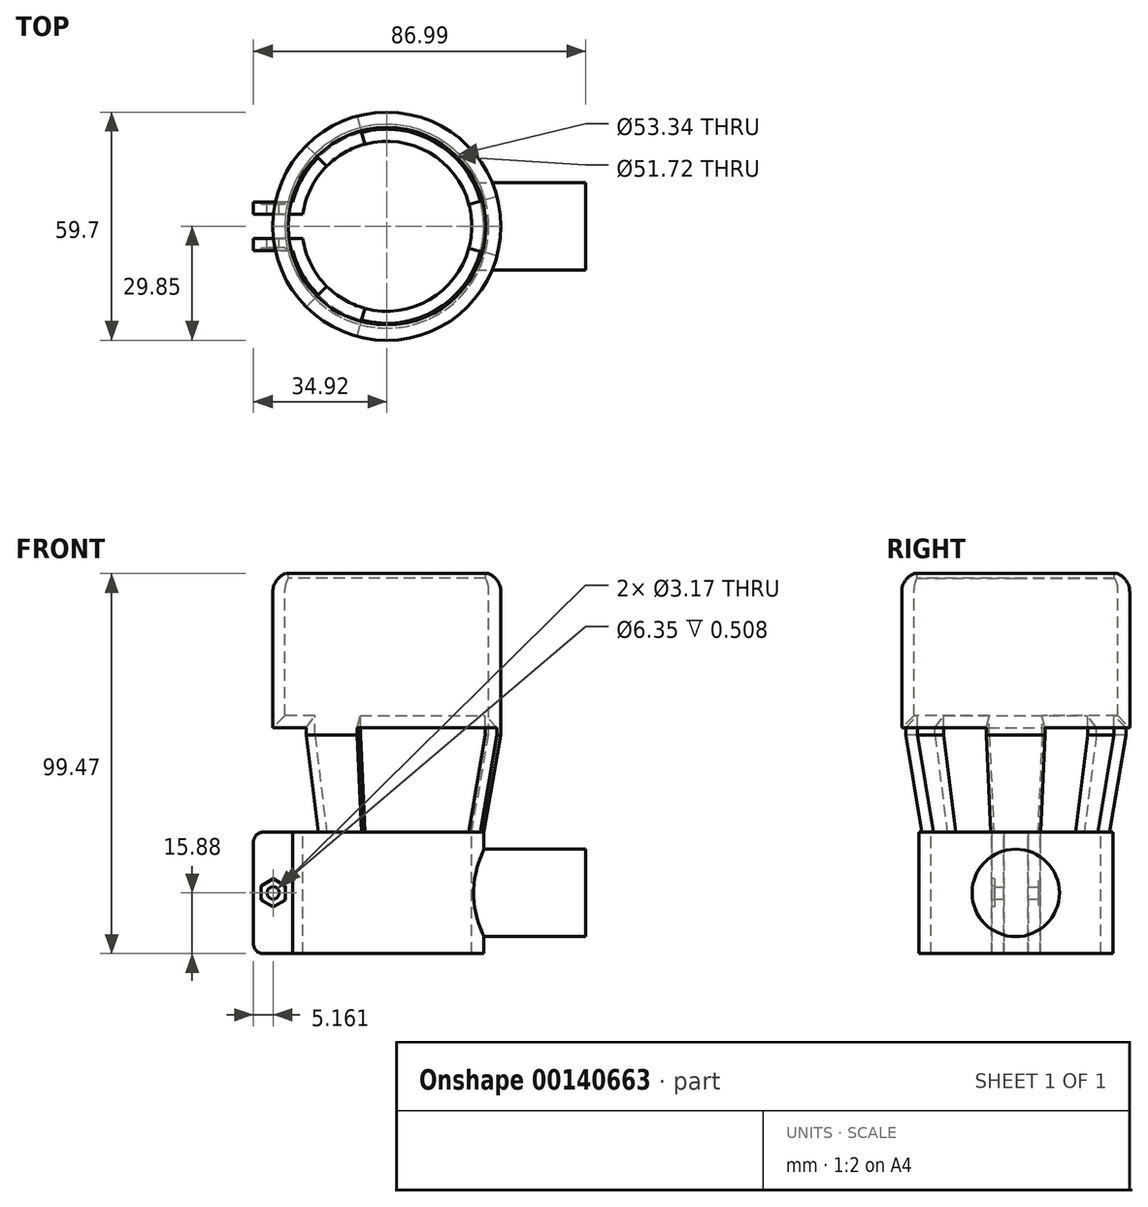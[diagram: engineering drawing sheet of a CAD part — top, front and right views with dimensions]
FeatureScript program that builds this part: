
annotation { "Feature Type Name" : "Feature", "Feature Type Description" : "" }
export const myFeature = defineFeature(function(context is Context, id is Id, definition is map)
    precondition{}
    {
        {
            var Q0;
            Q0=qCreatedBy(makeId("Front.planeOp"),FACE);
            var sketch = newSketch(context, id + "F0", { "sketchPlane" : qUnion([Q0])});
            skLineSegment(sketch, "E0.bottom", {"start": v(22.23, -15.87) * mm, "end": v(-22.23, -15.88) * mm});
            skLineSegment(sketch, "E0.top", {"start": v(22.22, 15.88) * mm, "end": v(-22.23, 15.87) * mm});
            skLineSegment(sketch, "E0.left", {"start": v(22.23, -15.87) * mm, "end": v(22.22, 15.88) * mm});
            skLineSegment(sketch, "E0.right", {"start": v(-22.23, -15.88) * mm, "end": v(-22.23, 15.88) * mm});
            skPoint(sketch, "E0.middle", {"position": v(0, 0) * mm});
            skLineSegment(sketch, "E1.top", {"start": v(26.67, 79.38) * mm, "end": v(-26.67, 79.38) * mm});
            skLineSegment(sketch, "E1.left", {"start": v(26.67, 41.28) * mm, "end": v(26.67, 79.38) * mm});
            skLineSegment(sketch, "E1.right", {"start": v(-26.67, 41.28) * mm, "end": v(-26.67, 79.38) * mm});
            skPoint(sketch, "E1.middle", {"position": v(0, 60.33) * mm});
            skPoint(sketch, "E2.middle", {"position": v(0, 38.1) * mm});
            skLineSegment(sketch, "E3", {"start": v(26.67, 79.38) * mm, "end": v(29.85, 79.38) * mm});
            skLineSegment(sketch, "E4", {"start": v(29.85, 79.38) * mm, "end": v(29.85, 41.28) * mm});
            skLineSegment(sketch, "E5", {"start": v(29.85, 41.27) * mm, "end": v(26.67, 41.27) * mm});
            skLineSegment(sketch, "E6", {"start": v(22.22, 15.88) * mm, "end": v(25.4, 15.88) * mm});
            skLineSegment(sketch, "E7", {"start": v(25.4, 15.88) * mm, "end": v(25.4, -15.87) * mm});
            skLineSegment(sketch, "E8", {"start": v(25.4, -15.87) * mm, "end": v(22.23, -15.87) * mm});
            skLineSegment(sketch, "E9", {"start": v(0, 79.38) * mm, "end": v(0, -15.88) * mm, "construction": true});
            skLineSegment(sketch, "E10.bottom", {"start": v(-39.6, -29.43) * mm, "end": v(-4.84, -29.43) * mm});
            skLineSegment(sketch, "E10.top", {"start": v(-39.6, 29.43) * mm, "end": v(-4.84, 29.43) * mm});
            skLineSegment(sketch, "E10.left", {"start": v(-39.6, -29.43) * mm, "end": v(-39.6, 29.43) * mm});
            skLineSegment(sketch, "E10.right", {"start": v(-4.84, -29.43) * mm, "end": v(-4.84, 29.43) * mm});
            skPoint(sketch, "E10.middle", {"position": v(-22.23, 0) * mm});
            skLineSegment(sketch, "E11", {"start": v(-22.23, 15.88) * mm, "end": v(-32.39, 15.88) * mm});
            skLineSegment(sketch, "E12", {"start": v(-34.93, 13.33) * mm, "end": v(-34.93, -13.34) * mm});
            skLineSegment(sketch, "E13", {"start": v(-32.38, -15.88) * mm, "end": v(-22.23, -15.88) * mm});
            skPoint(sketch, "E14.visualSharp", {"position": v(-34.93, 15.88) * mm});
            skArc(sketch, "E14.filletArc", {"start": v(-32.39, 15.88) * mm, "mid": v(-34.18, 15.13) * mm, "end": v(-34.93, 13.33) * mm});
            skPoint(sketch, "E15.visualSharp", {"position": v(-34.93, -15.88) * mm});
            skArc(sketch, "E15.filletArc", {"start": v(-34.93, -13.34) * mm, "mid": v(-34.18, -15.13) * mm, "end": v(-32.38, -15.88) * mm});
            skArc(sketch, "E16", {"start": v(26.67, 79.38) * mm, "mid": v(26.46, 80.9) * mm, "end": v(25.86, 82.31) * mm});
            skLineSegment(sketch, "E17", {"start": v(25.86, 82.31) * mm, "end": v(29.84, 82.31) * mm});
            skLineSegment(sketch, "E18", {"start": v(29.85, 82.31) * mm, "end": v(29.85, 79.38) * mm});
            skLineSegment(sketch, "E19", {"start": v(25.86, 82.31) * mm, "end": v(25.86, 83.76) * mm});
            skLineSegment(sketch, "E20", {"start": v(25.86, 83.76) * mm, "end": v(29.84, 83.76) * mm});
            skLineSegment(sketch, "E21", {"start": v(29.85, 83.76) * mm, "end": v(29.85, 82.31) * mm});
            skLineSegment(sketch, "E22", {"start": v(-26.67, 41.27) * mm, "end": v(26.67, 41.27) * mm});
            skPoint(sketch, "E23.start.orphan", {"position": v(60.32, 9.53) * mm});
            skPoint(sketch, "E24.end.orphan", {"position": v(25.4, 0) * mm});
            skPoint(sketch, "E24.start.orphan", {"position": v(22.23, 0) * mm});
            skPoint(sketch, "E25.start.orphan", {"position": v(22.22, 11.43) * mm});
            skLineSegment(sketch, "E26", {"start": v(22.22, 11.43) * mm, "end": v(25.4, 11.43) * mm});
            skLineSegment(sketch, "E27", {"start": v(25.4, 11.43) * mm, "end": v(52.07, 11.43) * mm});
            skLineSegment(sketch, "E28", {"start": v(52.07, 11.43) * mm, "end": v(52.07, 0) * mm});
            skLineSegment(sketch, "E29", {"start": v(52.07, 0) * mm, "end": v(25.4, 0) * mm});
            skLineSegment(sketch, "E30", {"start": v(22.23, 0) * mm, "end": v(25.4, 0) * mm});
            skSolve(sketch);
        }
        {
            var Q0;
            Q0=makeQuery(id+"F0.imprint","IMPRINT",FACE,{"disambiguationData":[TD([[makeQuery(id+"F0.imprint","IMPRINT",EDGE,{"derivedFrom":sQuery(id+"F0.wireOp",EDGE,"E1.left")}),-1.0]])]});
            var Q1;
            Q1=makeQuery(id+"F0.imprint","IMPRINT",FACE,{"disambiguationData":[TD([[makeQuery(id+"F0.imprint","IMPRINT",EDGE,{"derivedFrom":sQuery(id+"F0.wireOp",EDGE,"E0.left")}),-1.0]])]});
            var Q2;
            Q2=sQuery(id+"F0.wireOp",EDGE,"E9");
            revolve(context, id + "F1", {"entities" : qUnion([Q0, Q1]), "axis" : qUnion([Q2]), "revolveType" : RevolveType.TWO_DIRECTIONS, "angle" : 15 * degree, "angleBack" : 345 * degree});
        }
        {
            var Q0;
            Q0=makeQuery(id+"F1.opRevolve","SWEPT_FACE",FACE,{"disambiguationData":[OSD([sQuery(id+"F0.wireOp",EDGE,"E5")])]});
            var Q1;
            Q1=makeQuery(id+"F1.opRevolve","SWEPT_FACE",FACE,{"disambiguationData":[OSD([sQuery(id+"F0.wireOp",EDGE,"E6")])]});
            loft(context, id + "F2", {"sheetProfilesArray" : [{ "sheetProfileEntities" : qUnion([Q0]) }, { "sheetProfileEntities" : qUnion([Q1]) }]});
        }
        {
            var Q0;
            Q0=makeQuery(id+"F0.imprint","IMPRINT",FACE,{"disambiguationData":[TD([[makeQuery(id+"F0.imprint","IMPRINT",EDGE,{"derivedFrom":sQuery(id+"F0.wireOp",EDGE,"E1.left")}),-1.0]])]});
            var Q1;
            Q1=makeQuery(id+"F0.imprint","IMPRINT",FACE,{"disambiguationData":[TD([[makeQuery(id+"F0.imprint","IMPRINT",EDGE,{"derivedFrom":sQuery(id+"F0.wireOp",EDGE,"E0.left")}),-1.0]])]});
            var Q2;
            Q2=makeQuery(id+"F0.imprint","IMPRINT",FACE,{"disambiguationData":[TD([[makeQuery(id+"F0.imprint","IMPRINT",EDGE,{"derivedFrom":sQuery(id+"F0.wireOp",EDGE,"E3")}),1.0]])]});
            var Q3;
            Q3=makeQuery(id+"F0.imprint","IMPRINT",FACE,{"disambiguationData":[TD([[makeQuery(id+"F0.imprint","IMPRINT",EDGE,{"derivedFrom":sQuery(id+"F0.wireOp",EDGE,"E17")}),1.0]])]});
            var Q4;
            Q4=sQuery(id+"F0.wireOp",EDGE,"E9");
            revolve(context, id + "F3", {"entities" : qUnion([Q0, Q1, Q2, Q3]), "axis" : qUnion([Q4]), "revolveType" : RevolveType.FULL});
        }
        {
            var Q0;
            Q0=makeQuery(id+"F1.opRevolve","SWEPT_BODY",BODY,{"disambiguationData":[OSD([sQuery(id+"F0.wireOp",EDGE,"E1.left"),sQuery(id+"F0.wireOp",EDGE,"E3"),sQuery(id+"F0.wireOp",EDGE,"E4"),sQuery(id+"F0.wireOp",EDGE,"E5")])]});
            var Q1;
            Q1=makeQuery(id+"F3.opRevolve","SWEPT_BODY",BODY,{"disambiguationData":[OSD([sQuery(id+"F0.wireOp",EDGE,"E1.left"),sQuery(id+"F0.wireOp",EDGE,"E3"),sQuery(id+"F0.wireOp",EDGE,"E4"),sQuery(id+"F0.wireOp",EDGE,"E5")])]});
            booleanBodies(context, id + "F4", {"operationType" : BooleanOperationType.UNION, "tools" : qUnion([Q0, Q1])});
        }
        {
            var Q0;
            Q0=makeQuery(id+"F2.opLoft","SWEPT_BODY",BODY,{"disambiguationData":[OSD([sQuery(id+"F0.wireOp",EDGE,"E5"),sQuery(id+"F0.wireOp",EDGE,"E6")])]});
            var Q1;
            Q1=sQuery(id+"F0.wireOp",EDGE,"E9");
            circularPattern(context, id + "F5", {"entities" : qUnion([Q0]), "axis" : qUnion([Q1]), "angle" : 120 * degree, "instanceCount" : 3});
        }
        {
            var Q0;
            Q0=makeQuery(id+"F0.imprint","IMPRINT",FACE,{"disambiguationData":[TD([[makeQuery(id+"F0.imprint","IMPRINT",EDGE,{"derivedFrom":sQuery(id+"F0.wireOp",EDGE,"E12")}),1.0]])]});
            var Q1;
            {var subQ0=sQuery(id+"F0.wireOp",EDGE,"E0.right");Q1=makeQuery(id+"F0.imprint","IMPRINT",FACE,{"disambiguationData":[TD([[makeQuery(id+"F0.imprint","IMPRINT",EDGE,{"derivedFrom":subQ0}),1.0]])]});}
            extrude(context, id + "F6", {"entities" : qUnion([Q0, Q1]), "operationType" : NewBodyOperationType.ADD, "endBound" : BoundingType.SYMMETRIC, "depth" : 12.7 * mm});
        }
        {
            var Q0;
            {var subQ1=sQuery(id+"F0.wireOp",EDGE,"E10.top");Q0=makeQuery(id+"F0.imprint","IMPRINT",FACE,{"disambiguationData":[TD([[makeQuery(id+"F0.imprint","IMPRINT",EDGE,{"derivedFrom":subQ1}),-1.0]])]});}
            var Q1;
            {var subQ1=sQuery(id+"F0.wireOp",EDGE,"E10.bottom");Q1=makeQuery(id+"F0.imprint","IMPRINT",FACE,{"disambiguationData":[TD([[makeQuery(id+"F0.imprint","IMPRINT",EDGE,{"derivedFrom":subQ1}),1.0]])]});}
            var Q2;
            {var subQ0=sQuery(id+"F0.wireOp",EDGE,"E0.right");Q2=makeQuery(id+"F0.imprint","IMPRINT",FACE,{"disambiguationData":[TD([[makeQuery(id+"F0.imprint","IMPRINT",EDGE,{"derivedFrom":subQ0}),-1.0]])]});}
            var Q3;
            {var subQ0=sQuery(id+"F0.wireOp",EDGE,"E0.right");Q3=makeQuery(id+"F0.imprint","IMPRINT",FACE,{"disambiguationData":[TD([[makeQuery(id+"F0.imprint","IMPRINT",EDGE,{"derivedFrom":subQ0}),1.0]])]});}
            var Q4;
            Q4=makeQuery(id+"F0.imprint","IMPRINT",FACE,{"disambiguationData":[TD([[makeQuery(id+"F0.imprint","IMPRINT",EDGE,{"derivedFrom":sQuery(id+"F0.wireOp",EDGE,"E12")}),1.0]])]});
            extrude(context, id + "F7", {"entities" : qUnion([Q0, Q1, Q2, Q3, Q4]), "operationType" : NewBodyOperationType.REMOVE, "endBound" : BoundingType.SYMMETRIC, "depth" : 6.35 * mm});
        }
        {
            var Q0;
            Q0=makeQuery(id+"F6.opExtrude","CAP_FACE",FACE,{"disambiguationData":[OSD([sQuery(id+"F0.wireOp",EDGE,"E0.right"),sQuery(id+"F0.wireOp",EDGE,"E11"),sQuery(id+"F0.wireOp",EDGE,"E12"),sQuery(id+"F0.wireOp",EDGE,"E13"),sQuery(id+"F0.wireOp",EDGE,"E14.filletArc"),sQuery(id+"F0.wireOp",EDGE,"E15.filletArc")])],"isStart":true});
            var sketch = newSketch(context, id + "F8", { "sketchPlane" : qUnion([Q0])});
            skLineSegment(sketch, "E31", {"start": v(24.6, 0) * mm, "end": v(34.93, 0) * mm});
            skLineSegment(sketch, "E32", {"start": v(29.76, 15.88) * mm, "end": v(29.76, 0) * mm});
            skLineSegment(sketch, "E33", {"start": v(29.76, 0) * mm, "end": v(29.76, -15.88) * mm});
            skSolve(sketch);
        }
        {
            var Q0;
            Q0=sQuery(id+"F8.wireOp",VERTEX,"E33.start");
            var Q1;
            Q1=makeQuery(id+"F3.opRevolve","SWEPT_BODY",BODY,{"disambiguationData":[OSD([sQuery(id+"F0.wireOp",EDGE,"E0.left"),sQuery(id+"F0.wireOp",EDGE,"E6"),sQuery(id+"F0.wireOp",EDGE,"E7"),sQuery(id+"F0.wireOp",EDGE,"E8")])]});
            hole(context, id + "F9", {"style" : HoleStyle.C_BORE, "endStyle" : HoleEndStyle.THROUGH, "holeDiameter" : 3.17 * mm, "cBoreDiameter" : 6.35 * mm, "cBoreDepth" : 0.5 * mm, "locations" : qUnion([Q0]), "scope" : qUnion([Q1]), "isTappedThrough" : true});
        }
        {
            var Q0;
            Q0=makeQuery(id+"F6.opExtrude","CAP_FACE",FACE,{"disambiguationData":[OSD([sQuery(id+"F0.wireOp",EDGE,"E0.right"),sQuery(id+"F0.wireOp",EDGE,"E11"),sQuery(id+"F0.wireOp",EDGE,"E12"),sQuery(id+"F0.wireOp",EDGE,"E13"),sQuery(id+"F0.wireOp",EDGE,"E14.filletArc"),sQuery(id+"F0.wireOp",EDGE,"E15.filletArc")])],"isStart":false});
            var sketch = newSketch(context, id + "F10", { "sketchPlane" : qUnion([Q0])});
            skCircle(sketch, "E34.cCircle", {"center": v(-29.76, 0) * mm, "radius": 3.18 * mm, "construction": true});
            skLineSegment(sketch, "E34.0", {"start": v(-26.58, -1.83) * mm, "end": v(-29.76, -3.67) * mm});
            skLineSegment(sketch, "E34.1", {"start": v(-29.76, -3.67) * mm, "end": v(-32.93, -1.83) * mm});
            skLineSegment(sketch, "E34.2", {"start": v(-32.93, -1.83) * mm, "end": v(-32.93, 1.83) * mm});
            skLineSegment(sketch, "E34.3", {"start": v(-32.93, 1.83) * mm, "end": v(-29.76, 3.67) * mm});
            skLineSegment(sketch, "E34.4", {"start": v(-29.76, 3.67) * mm, "end": v(-26.58, 1.83) * mm});
            skLineSegment(sketch, "E34.5", {"start": v(-26.58, 1.83) * mm, "end": v(-26.58, -1.83) * mm});
            skPoint(sketch, "E34.0.midPoint", {"position": v(-28.17, -2.75) * mm});
            skSolve(sketch);
        }
        {
            var Q0;
            Q0=makeQuery(id+"F10.imprint","IMPRINT",FACE,{"disambiguationData":[TD([[makeQuery(id+"F10.imprint","IMPRINT",EDGE,{"derivedFrom":sQuery(id+"F10.wireOp",EDGE,"E34.0")}),-1.0]])]});
            extrude(context, id + "F11", {"entities" : qUnion([Q0]), "operationType" : NewBodyOperationType.REMOVE, "oppositeDirection" : true, "depth" : 0.76 * mm});
        }
        {
            var Q0;
            Q0=makeQuery(id+"F3.opRevolve","SWEPT_EDGE",EDGE,{"disambiguationData":[OSD([sQuery(id+"F0.wireOp",EDGE,"E20"),sQuery(id+"F0.wireOp",EDGE,"E21")])]});
            fillet(context, id + "F12", {"entities" : qUnion([Q0]), "radius" : 5.08 * mm, "tangentPropagation" : true, "allowEdgeOverflow" : false});
        }
        {
            var Q0;
            Q0=makeQuery(id+"F12.opFillet","BLEND_EDGE",EDGE,{"blendedFrom":[makeQuery(id+"F3.opRevolve","SWEPT_EDGE",EDGE,{"disambiguationData":[OSD([sQuery(id+"F0.wireOp",EDGE,"E20"),sQuery(id+"F0.wireOp",EDGE,"E21")])]}),makeQuery(id+"F3.opRevolve","SWEPT_FACE",FACE,{"disambiguationData":[OSD([sQuery(id+"F0.wireOp",EDGE,"E19")])]})],"blendedInto":[makeQuery(id+"F3.opRevolve","SWEPT_FACE",FACE,{"disambiguationData":[OSD([sQuery(id+"F0.wireOp",EDGE,"E19")])]})]});
            fillet(context, id + "F13", {"entities" : qUnion([Q0]), "radius" : 0.5 * mm, "tangentPropagation" : true, "allowEdgeOverflow" : false});
        }
        {
            var Q0;
            Q0=makeQuery(id+"F3.opRevolve","SWEPT_BODY",BODY,{"disambiguationData":[OSD([sQuery(id+"F0.wireOp",EDGE,"E0.left"),sQuery(id+"F0.wireOp",EDGE,"E6"),sQuery(id+"F0.wireOp",EDGE,"E7"),sQuery(id+"F0.wireOp",EDGE,"E8")])]});
            var Q1;
            Q1=makeQuery(id+"F5.opPattern","COPY",BODY,{"derivedFrom":makeQuery(id+"F2.opLoft","SWEPT_BODY",BODY,{"disambiguationData":[OSD([sQuery(id+"F0.wireOp",EDGE,"E5"),sQuery(id+"F0.wireOp",EDGE,"E6")])]}),"instanceName":"2"});
            var Q2;
            Q2=makeQuery(id+"F1.opRevolve","SWEPT_BODY",BODY,{"disambiguationData":[OSD([sQuery(id+"F0.wireOp",EDGE,"E1.left"),sQuery(id+"F0.wireOp",EDGE,"E3"),sQuery(id+"F0.wireOp",EDGE,"E4"),sQuery(id+"F0.wireOp",EDGE,"E5")])]});
            var Q3;
            Q3=makeQuery(id+"F5.opPattern","COPY",BODY,{"derivedFrom":makeQuery(id+"F2.opLoft","SWEPT_BODY",BODY,{"disambiguationData":[OSD([sQuery(id+"F0.wireOp",EDGE,"E5"),sQuery(id+"F0.wireOp",EDGE,"E6")])]}),"instanceName":"1"});
            var Q4;
            Q4=makeQuery(id+"F2.opLoft","SWEPT_BODY",BODY,{"disambiguationData":[OSD([sQuery(id+"F0.wireOp",EDGE,"E5"),sQuery(id+"F0.wireOp",EDGE,"E6")])]});
            booleanBodies(context, id + "F14", {"operationType" : BooleanOperationType.UNION, "tools" : qUnion([Q0, Q1, Q2, Q3, Q4])});
        }
        {
            var Q0;
            {var subQ0=sQuery(id+"F0.wireOp",EDGE,"E5");var subQ1=sQuery(id+"F0.wireOp",EDGE,"E1.left");var subQ2=sQuery(id+"F0.wireOp",EDGE,"E22");var subQ3=sQuery(id+"F0.wireOp",EDGE,"E6");var subQ4=sQuery(id+"F0.wireOp",EDGE,"E0.left");var subQ5=sQuery(id+"F0.wireOp",EDGE,"E0.top");var subQ7=sQuery(id+"F0.wireOp",EDGE,"E7");var subQ8=sQuery(id+"F0.wireOp",EDGE,"E4");Q0=makeQuery(id+"F14.opBoolean","SPLIT",EDGE,{"disambiguationData":[TD([makeQuery(id+"F5.opPattern","COPY",FACE,{"derivedFrom":makeQuery(id+"F2.opLoft","SWEPT_FACE",FACE,{"disambiguationData":[OSD([subQ5,subQ4,subQ1,subQ8,subQ0,subQ3,subQ7,subQ2]),TDD([makeQuery(id+"F1.opRevolve","CAP_VERTEX",VERTEX,{"disambiguationData":[OSD([subQ5,subQ4,subQ3])],"isStart":false}),makeQuery(id+"F1.opRevolve","CAP_VERTEX",VERTEX,{"disambiguationData":[OSD([subQ1,subQ0,subQ2])],"isStart":false}),makeQuery(id+"F1.opRevolve","CAP_VERTEX",VERTEX,{"disambiguationData":[OSD([subQ8,subQ0])],"isStart":false}),makeQuery(id+"F1.opRevolve","CAP_VERTEX",VERTEX,{"disambiguationData":[OSD([subQ3,subQ7])],"isStart":false}),makeQuery(id+"F1.opRevolve","CAP_EDGE",EDGE,{"disambiguationData":[OSD([subQ0])],"isStart":false}),makeQuery(id+"F1.opRevolve","CAP_EDGE",EDGE,{"disambiguationData":[OSD([subQ3])],"isStart":false})])]}),"instanceName":"1"})])],"derivedFrom":makeQuery(id+"F4.opBoolean","MERGE",EDGE,{"derivedFrom":[makeQuery(id+"F1.opRevolve","SWEPT_EDGE",EDGE,{"disambiguationData":[OSD([subQ1,subQ0,subQ2])]}),makeQuery(id+"F3.opRevolve","SWEPT_EDGE",EDGE,{"disambiguationData":[OSD([subQ1,subQ0,subQ2])]})]})});}
            var Q1;
            {var subQ0=sQuery(id+"F0.wireOp",EDGE,"E6");var subQ1=sQuery(id+"F0.wireOp",EDGE,"E5");var subQ2=sQuery(id+"F0.wireOp",EDGE,"E7");var subQ3=sQuery(id+"F0.wireOp",EDGE,"E4");var subQ4=sQuery(id+"F0.wireOp",EDGE,"E22");var subQ5=sQuery(id+"F0.wireOp",EDGE,"E1.left");var subQ6=sQuery(id+"F0.wireOp",EDGE,"E0.left");var subQ7=sQuery(id+"F0.wireOp",EDGE,"E0.top");Q1=makeQuery(id+"F14.opBoolean","SPLIT",EDGE,{"disambiguationData":[TD([makeQuery(id+"F2.opLoft","SWEPT_FACE",FACE,{"disambiguationData":[OSD([subQ7,subQ6,subQ5,subQ3,subQ1,subQ0,subQ2,subQ4]),TDD([makeQuery(id+"F1.opRevolve","CAP_VERTEX",VERTEX,{"disambiguationData":[OSD([subQ7,subQ6,subQ0])],"isStart":false}),makeQuery(id+"F1.opRevolve","CAP_VERTEX",VERTEX,{"disambiguationData":[OSD([subQ5,subQ1,subQ4])],"isStart":false}),makeQuery(id+"F1.opRevolve","CAP_VERTEX",VERTEX,{"disambiguationData":[OSD([subQ3,subQ1])],"isStart":false}),makeQuery(id+"F1.opRevolve","CAP_VERTEX",VERTEX,{"disambiguationData":[OSD([subQ0,subQ2])],"isStart":false}),makeQuery(id+"F1.opRevolve","CAP_EDGE",EDGE,{"disambiguationData":[OSD([subQ1])],"isStart":false}),makeQuery(id+"F1.opRevolve","CAP_EDGE",EDGE,{"disambiguationData":[OSD([subQ0])],"isStart":false})])]})])],"derivedFrom":makeQuery(id+"F4.opBoolean","MERGE",EDGE,{"derivedFrom":[makeQuery(id+"F1.opRevolve","SWEPT_EDGE",EDGE,{"disambiguationData":[OSD([subQ5,subQ1,subQ4])]}),makeQuery(id+"F3.opRevolve","SWEPT_EDGE",EDGE,{"disambiguationData":[OSD([subQ5,subQ1,subQ4])]})]})});}
            var Q2;
            {var subQ0=sQuery(id+"F0.wireOp",EDGE,"E6");var subQ1=sQuery(id+"F0.wireOp",EDGE,"E5");var subQ2=sQuery(id+"F0.wireOp",EDGE,"E7");var subQ3=sQuery(id+"F0.wireOp",EDGE,"E4");var subQ4=sQuery(id+"F0.wireOp",EDGE,"E22");var subQ5=sQuery(id+"F0.wireOp",EDGE,"E1.left");var subQ6=sQuery(id+"F0.wireOp",EDGE,"E0.left");var subQ7=sQuery(id+"F0.wireOp",EDGE,"E0.top");Q2=makeQuery(id+"F14.opBoolean","SPLIT",EDGE,{"disambiguationData":[TD([makeQuery(id+"F2.opLoft","SWEPT_FACE",FACE,{"disambiguationData":[OSD([subQ7,subQ6,subQ5,subQ3,subQ1,subQ0,subQ2,subQ4]),TDD([makeQuery(id+"F1.opRevolve","CAP_VERTEX",VERTEX,{"disambiguationData":[OSD([subQ7,subQ6,subQ0])],"isStart":true}),makeQuery(id+"F1.opRevolve","CAP_VERTEX",VERTEX,{"disambiguationData":[OSD([subQ5,subQ1,subQ4])],"isStart":true}),makeQuery(id+"F1.opRevolve","CAP_VERTEX",VERTEX,{"disambiguationData":[OSD([subQ3,subQ1])],"isStart":true}),makeQuery(id+"F1.opRevolve","CAP_VERTEX",VERTEX,{"disambiguationData":[OSD([subQ0,subQ2])],"isStart":true}),makeQuery(id+"F1.opRevolve","CAP_EDGE",EDGE,{"disambiguationData":[OSD([subQ1])],"isStart":true}),makeQuery(id+"F1.opRevolve","CAP_EDGE",EDGE,{"disambiguationData":[OSD([subQ0])],"isStart":true})])]})])],"derivedFrom":makeQuery(id+"F4.opBoolean","MERGE",EDGE,{"derivedFrom":[makeQuery(id+"F1.opRevolve","SWEPT_EDGE",EDGE,{"disambiguationData":[OSD([subQ5,subQ1,subQ4])]}),makeQuery(id+"F3.opRevolve","SWEPT_EDGE",EDGE,{"disambiguationData":[OSD([subQ5,subQ1,subQ4])]})]})});}
            chamfer(context, id + "F15", {"entities" : qUnion([Q0, Q1, Q2]), "width" : 5.08 * mm, "tangentPropagation" : true});
        }
        {
            var Q0;
            {var subQ0=sQuery(id+"F0.wireOp",EDGE,"E27");Q0=makeQuery(id+"F0.imprint","IMPRINT",FACE,{"disambiguationData":[TD([[makeQuery(id+"F0.imprint","IMPRINT",EDGE,{"derivedFrom":subQ0}),-1.0]])]});}
            var Q1;
            {var subQ0=sQuery(id+"F0.wireOp",EDGE,"E26");Q1=makeQuery(id+"F0.imprint","IMPRINT",FACE,{"disambiguationData":[TD([[makeQuery(id+"F0.imprint","IMPRINT",EDGE,{"derivedFrom":subQ0}),-1.0]])]});}
            var Q2;
            Q2=sQuery(id+"F0.wireOp",EDGE,"E29");
            revolve(context, id + "F16", {"operationType" : NewBodyOperationType.ADD, "entities" : qUnion([Q0, Q1]), "axis" : qUnion([Q2]), "revolveType" : RevolveType.FULL});
        }
    });
